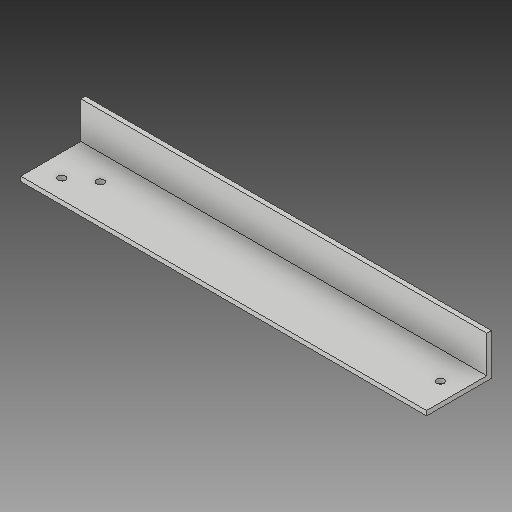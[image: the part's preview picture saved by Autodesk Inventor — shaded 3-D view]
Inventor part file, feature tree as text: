
AUTODESK INVENTOR PART (.ipt)
format: ipt  version: 2018 (Build 220112000, 112)  size: 109,056 bytes
history: native  units: in
note: dims shown in document units (in); Inventor stores cm internally (conversion verified against a paired STEP export)
features: sketch x4, other x3
ambient origin geometry x8: Origin, YZ Plane, XZ Plane, XY Plane, X Axis, Y Axis, Z Axis, Center Point
bodies: Solid1 (feature_tree)
feature tree (7):
  other  "angle iron with  holes 2.ipt"
  other  "Solid1::angle iron with  holes 2.ipt"
  other  "TaggingFeature1"
  sketch  "Sketch1"  dims[d0=0.3937in]
  sketch  "Sketch2"
  sketch  "Sketch3"
  sketch  "Sketch4"
